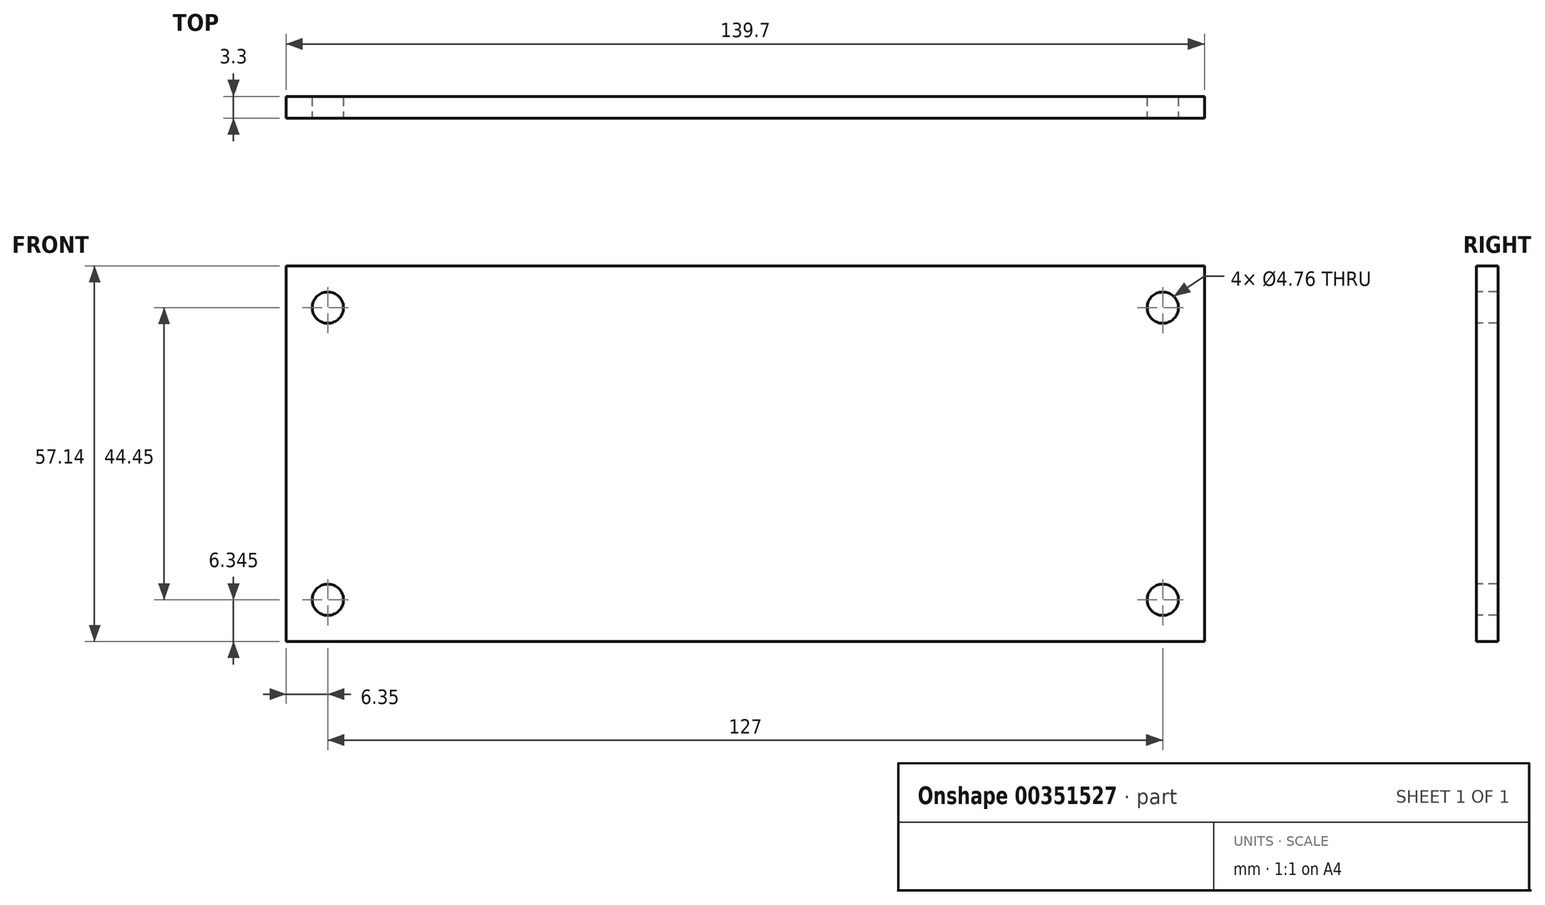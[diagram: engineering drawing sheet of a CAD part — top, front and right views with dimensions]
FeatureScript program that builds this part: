
annotation { "Feature Type Name" : "Feature", "Feature Type Description" : "" }
export const myFeature = defineFeature(function(context is Context, id is Id, definition is map)
    precondition{}
    {
        {
            var Q0;
            Q0=qCreatedBy(makeId("Front.planeOp"),FACE);
            var sketch = newSketch(context, id + "F0", { "sketchPlane" : qUnion([Q0])});
            skLineSegment(sketch, "E0.bottom", {"start": v(69.85, 28.58) * mm, "end": v(-69.85, 28.58) * mm});
            skLineSegment(sketch, "E0.top", {"start": v(69.85, -28.57) * mm, "end": v(-69.85, -28.57) * mm});
            skLineSegment(sketch, "E0.left", {"start": v(69.85, 28.58) * mm, "end": v(69.85, -28.57) * mm});
            skLineSegment(sketch, "E0.right", {"start": v(-69.85, 28.58) * mm, "end": v(-69.85, -28.57) * mm});
            skPoint(sketch, "E0.middle", {"position": v(0, 0) * mm});
            skSolve(sketch);
        }
        {
            var Q0;
            Q0 = qSketchRegion(id + "F0", true);
            extrude(context, id + "F1", {"entities" : qUnion([Q0]), "depth" : 3.3 * mm, "symmetric" : true});
        }
        {
            var Q0;
            Q0=makeQuery(id+"F1.opExtrude","CAP_FACE",FACE,{"disambiguationData":[OSD([sQuery(id+"F0.wireOp",EDGE,"E0.bottom"),sQuery(id+"F0.wireOp",EDGE,"E0.top"),sQuery(id+"F0.wireOp",EDGE,"E0.left"),sQuery(id+"F0.wireOp",EDGE,"E0.right")])],"isStart":false});
            var sketch = newSketch(context, id + "F2", { "sketchPlane" : qUnion([Q0])});
            skCircle(sketch, "E1", {"center": v(-63.5, 22.23) * mm, "radius": 2.38 * mm});
            skCircle(sketch, "E2", {"center": v(-63.5, -22.22) * mm, "radius": 2.38 * mm});
            skCircle(sketch, "E3", {"center": v(63.5, 22.23) * mm, "radius": 2.38 * mm});
            skCircle(sketch, "E4", {"center": v(63.5, -22.22) * mm, "radius": 2.38 * mm});
            skSolve(sketch);
        }
        {
            var Q0;
            Q0 = qSketchRegion(id + "F2", true);
            var Q1;
            Q1=makeQuery(id+"F1.opExtrude","CAP_FACE",FACE,{"disambiguationData":[OSD([sQuery(id+"F0.wireOp",EDGE,"E0.bottom"),sQuery(id+"F0.wireOp",EDGE,"E0.top"),sQuery(id+"F0.wireOp",EDGE,"E0.left"),sQuery(id+"F0.wireOp",EDGE,"E0.right")])],"isStart":true});
            extrude(context, id + "F3", {"entities" : qUnion([Q0]), "operationType" : NewBodyOperationType.REMOVE, "endBound" : BoundingType.UP_TO_SURFACE, "oppositeDirection" : true, "endBoundEntityFace" : qUnion([Q1]), "depth" : 25.4 * mm});
        }
    });
